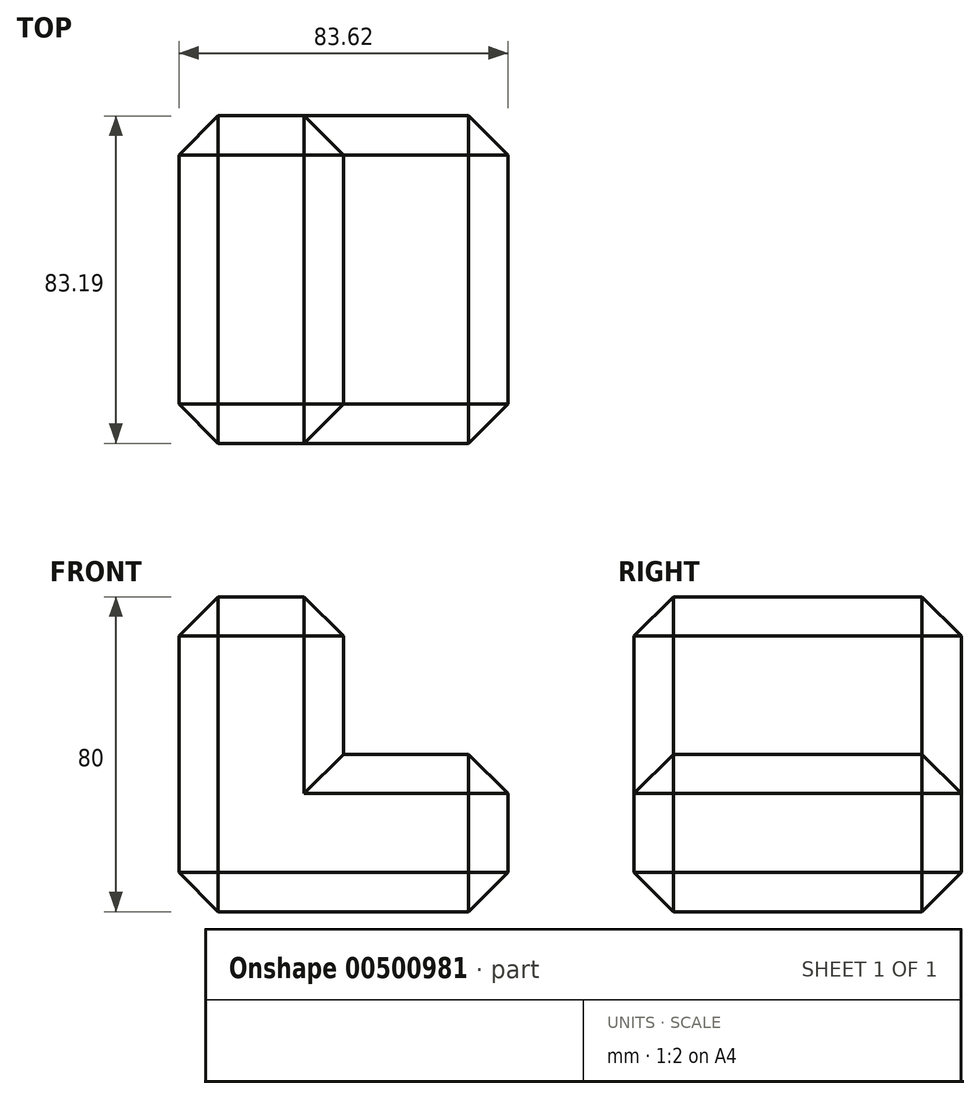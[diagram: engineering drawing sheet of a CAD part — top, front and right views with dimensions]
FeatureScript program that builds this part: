
annotation { "Feature Type Name" : "Feature", "Feature Type Description" : "" }
export const myFeature = defineFeature(function(context is Context, id is Id, definition is map)
    precondition{}
    {
        {
            var Q0;
            Q0=qCreatedBy(makeId("Top.planeOp"),FACE);
            var sketch = newSketch(context, id + "F0", { "sketchPlane" : qUnion([Q0])});
            skLineSegment(sketch, "E0.bottom", {"start": v(-59.13, -45.93) * mm, "end": v(24.5, -45.93) * mm});
            skLineSegment(sketch, "E0.top", {"start": v(-59.13, 37.26) * mm, "end": v(24.5, 37.26) * mm});
            skLineSegment(sketch, "E0.left", {"start": v(-59.13, -45.93) * mm, "end": v(-59.13, 37.26) * mm});
            skLineSegment(sketch, "E0.right", {"start": v(24.5, -45.93) * mm, "end": v(24.5, 37.26) * mm});
            skSolve(sketch);
        }
        {
            var Q0;
            Q0=makeQuery(id+"F0.imprint","IMPRINT",FACE,{"disambiguationData":[TD([[makeQuery(id+"F0.imprint","IMPRINT",EDGE,{"derivedFrom":sQuery(id+"F0.wireOp",EDGE,"E0.bottom")}),1.0]])]});
            extrude(context, id + "F1", {"entities" : qUnion([Q0]), "depth" : 40 * mm});
        }
        {
            var Q0;
            Q0=makeQuery(id+"F1.opExtrude","CAP_FACE",FACE,{"disambiguationData":[OSD([sQuery(id+"F0.wireOp",EDGE,"E0.bottom"),sQuery(id+"F0.wireOp",EDGE,"E0.top"),sQuery(id+"F0.wireOp",EDGE,"E0.left"),sQuery(id+"F0.wireOp",EDGE,"E0.right")])],"isStart":false});
            var sketch = newSketch(context, id + "F2", { "sketchPlane" : qUnion([Q0])});
            skLineSegment(sketch, "E1", {"start": v(-17.32, 37.26) * mm, "end": v(-17.32, -45.93) * mm});
            skSolve(sketch);
        }
        {
            var Q0;
            {var subQ1=sQuery(id+"F2.wireOp",EDGE,"E1");Q0=makeQuery(id+"F2.imprint","IMPRINT",FACE,{"disambiguationData":[TD([[makeQuery(id+"F2.imprint","IMPRINT",EDGE,{"derivedFrom":subQ1}),-1.0]])]});}
            extrude(context, id + "F3", {"entities" : qUnion([Q0]), "operationType" : NewBodyOperationType.ADD, "depth" : 40 * mm});
        }
        {
            var Q0;
            Q0=makeQuery(id+"F3.opExtrude","CAP_EDGE",EDGE,{"disambiguationData":[OSD([sQuery(id+"F2.wireOp",EDGE,"E1")])],"isStart":false});
            var Q1;
            Q1=makeQuery(id+"F3.opExtrude","CAP_EDGE",EDGE,{"disambiguationData":[OSD([sQuery(id+"F0.wireOp",EDGE,"E0.bottom")])],"isStart":false});
            var Q2;
            Q2=makeQuery(id+"F3.opExtrude","CAP_EDGE",EDGE,{"disambiguationData":[OSD([sQuery(id+"F0.wireOp",EDGE,"E0.left")])],"isStart":false});
            var Q3;
            Q3=makeQuery(id+"F3.opExtrude","CAP_EDGE",EDGE,{"disambiguationData":[OSD([sQuery(id+"F0.wireOp",EDGE,"E0.top")])],"isStart":false});
            var Q4;
            Q4=makeQuery(id+"F3.opExtrude","SWEPT_EDGE",EDGE,{"disambiguationData":[OSD([sQuery(id+"F0.wireOp",EDGE,"E0.bottom"),sQuery(id+"F2.wireOp",EDGE,"E1")])]});
            var Q5;
            Q5=makeQuery(id+"F3.opExtrude","CAP_EDGE",EDGE,{"disambiguationData":[OSD([sQuery(id+"F2.wireOp",EDGE,"E1")])],"isStart":true});
            var Q6;
            Q6=makeQuery(id+"F3.opExtrude","SWEPT_EDGE",EDGE,{"disambiguationData":[OSD([sQuery(id+"F0.wireOp",EDGE,"E0.top"),sQuery(id+"F2.wireOp",EDGE,"E1")])]});
            var Q7;
            Q7=makeQuery(id+"F1.opExtrude","CAP_EDGE",EDGE,{"disambiguationData":[OSD([sQuery(id+"F0.wireOp",EDGE,"E0.top")])],"isStart":false});
            var Q8;
            Q8=makeQuery(id+"F1.opExtrude","CAP_EDGE",EDGE,{"disambiguationData":[OSD([sQuery(id+"F0.wireOp",EDGE,"E0.bottom")])],"isStart":false});
            var Q9;
            Q9=makeQuery(id+"F1.opExtrude","CAP_EDGE",EDGE,{"disambiguationData":[OSD([sQuery(id+"F0.wireOp",EDGE,"E0.right")])],"isStart":false});
            var Q10;
            Q10=makeQuery(id+"F1.opExtrude","SWEPT_EDGE",EDGE,{"disambiguationData":[OSD([sQuery(id+"F0.wireOp",EDGE,"E0.bottom"),sQuery(id+"F0.wireOp",EDGE,"E0.right")])]});
            var Q11;
            Q11=makeQuery(id+"F1.opExtrude","SWEPT_EDGE",EDGE,{"disambiguationData":[OSD([sQuery(id+"F0.wireOp",EDGE,"E0.top"),sQuery(id+"F0.wireOp",EDGE,"E0.right")])]});
            var Q12;
            Q12=makeQuery(id+"F1.opExtrude","CAP_EDGE",EDGE,{"disambiguationData":[OSD([sQuery(id+"F0.wireOp",EDGE,"E0.right")])],"isStart":true});
            var Q13;
            Q13=makeQuery(id+"F1.opExtrude","CAP_EDGE",EDGE,{"disambiguationData":[OSD([sQuery(id+"F0.wireOp",EDGE,"E0.bottom")])],"isStart":true});
            var Q14;
            {var subQ0=sQuery(id+"F0.wireOp",EDGE,"E0.left");var subQ1=sQuery(id+"F0.wireOp",EDGE,"E0.bottom");Q14=makeQuery(id+"F3.boolean.opBoolean","MERGE",EDGE,{"derivedFrom":[makeQuery(id+"F1.opExtrude","SWEPT_EDGE",EDGE,{"disambiguationData":[OSD([subQ1,subQ0])]}),makeQuery(id+"F3.opExtrude","SWEPT_EDGE",EDGE,{"disambiguationData":[OSD([subQ1,subQ0])]})]});}
            var Q15;
            Q15=makeQuery(id+"F1.opExtrude","CAP_EDGE",EDGE,{"disambiguationData":[OSD([sQuery(id+"F0.wireOp",EDGE,"E0.left")])],"isStart":true});
            var Q16;
            Q16=makeQuery(id+"F1.opExtrude","CAP_EDGE",EDGE,{"disambiguationData":[OSD([sQuery(id+"F0.wireOp",EDGE,"E0.top")])],"isStart":true});
            var Q17;
            {var subQ0=sQuery(id+"F0.wireOp",EDGE,"E0.left");var subQ1=sQuery(id+"F0.wireOp",EDGE,"E0.top");Q17=makeQuery(id+"F3.boolean.opBoolean","MERGE",EDGE,{"derivedFrom":[makeQuery(id+"F1.opExtrude","SWEPT_EDGE",EDGE,{"disambiguationData":[OSD([subQ1,subQ0])]}),makeQuery(id+"F3.opExtrude","SWEPT_EDGE",EDGE,{"disambiguationData":[OSD([subQ1,subQ0])]})]});}
            chamfer(context, id + "F4", {"entities" : qUnion([Q0, Q1, Q2, Q3, Q4, Q5, Q6, Q7, Q8, Q9, Q10, Q11, Q12, Q13, Q14, Q15, Q16, Q17]), "width" : 10 * mm, "tangentPropagation" : true});
        }
    });
